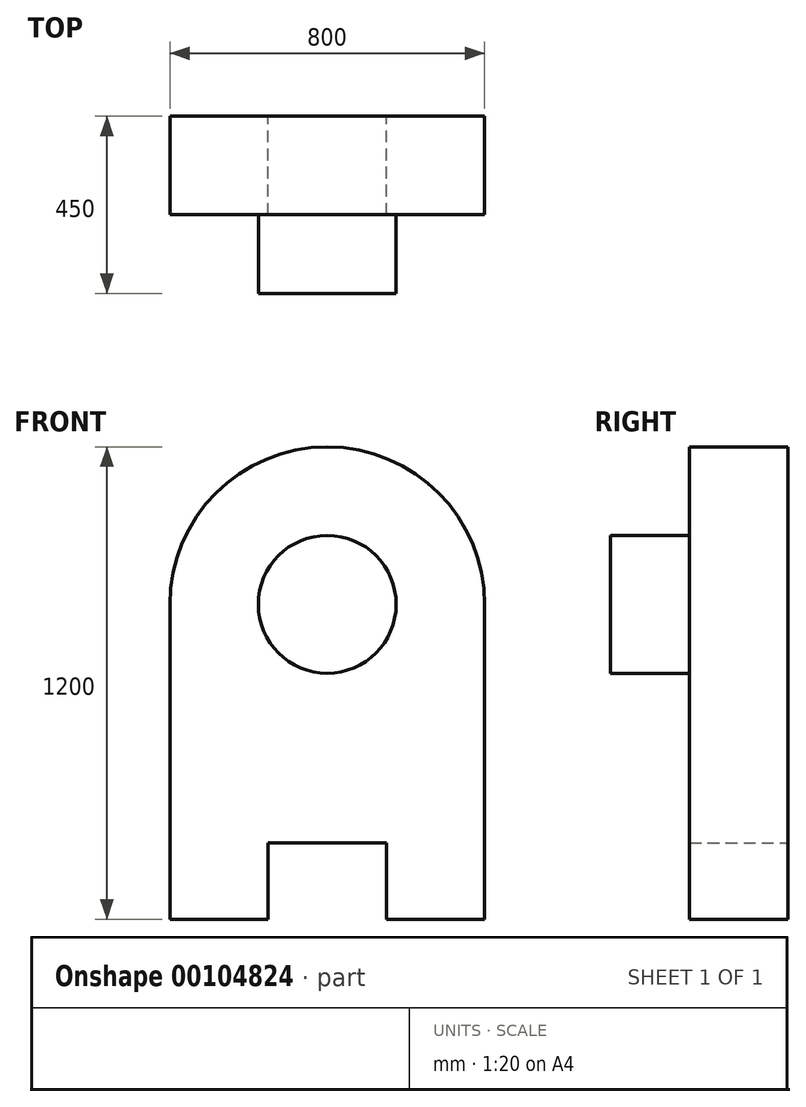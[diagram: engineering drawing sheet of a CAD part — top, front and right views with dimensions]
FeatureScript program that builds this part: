
annotation { "Feature Type Name" : "Feature", "Feature Type Description" : "" }
export const myFeature = defineFeature(function(context is Context, id is Id, definition is map)
    precondition{}
    {
        {
            var Q0;
            Q0=qCreatedBy(makeId("Front.planeOp"),FACE);
            var sketch = newSketch(context, id + "F0", { "sketchPlane" : qUnion([Q0])});
            skArc(sketch, "E0", {"start": v(400, 0) * mm, "mid": v(0, 400) * mm, "end": v(-400, 0) * mm});
            skLineSegment(sketch, "E1.bottom", {"start": v(-400, -800) * mm, "end": v(-150, -800) * mm});
            skLineSegment(sketch, "E1.left", {"start": v(-400, -800) * mm, "end": v(-400, 0) * mm});
            skLineSegment(sketch, "E1.right", {"start": v(400, -800) * mm, "end": v(400, 0) * mm});
            skPoint(sketch, "E1.top.end.orphan", {"position": v(400, 800) * mm});
            skPoint(sketch, "E2.orphan", {"position": v(-400, 800) * mm});
            skLineSegment(sketch, "E3", {"start": v(-150, -800) * mm, "end": v(-150, -606.18) * mm});
            skLineSegment(sketch, "E4", {"start": v(-150, -606.18) * mm, "end": v(150, -606.18) * mm});
            skLineSegment(sketch, "E5", {"start": v(150, -606.18) * mm, "end": v(150, -800) * mm});
            skPoint(sketch, "E6.end.orphan", {"position": v(168.48, -800) * mm});
            skLineSegment(sketch, "E7", {"start": v(150, -800) * mm, "end": v(400, -800) * mm});
            skSolve(sketch);
        }
        {
            var Q0;
            Q0 = qSketchRegion(id + "F0", true);
            extrude(context, id + "F1", {"entities" : qUnion([Q0]), "depth" : 250 * mm});
        }
        {
            var Q0;
            Q0=makeQuery(id+"F1.opExtrude","CAP_FACE",FACE,{"disambiguationData":[OSD([sQuery(id+"F0.wireOp",EDGE,"E0"),sQuery(id+"F0.wireOp",EDGE,"E1.bottom"),sQuery(id+"F0.wireOp",EDGE,"E1.left"),sQuery(id+"F0.wireOp",EDGE,"E1.right"),sQuery(id+"F0.wireOp",EDGE,"E3"),sQuery(id+"F0.wireOp",EDGE,"E4"),sQuery(id+"F0.wireOp",EDGE,"E5"),sQuery(id+"F0.wireOp",EDGE,"E7")])],"isStart":false});
            var sketch = newSketch(context, id + "F2", { "sketchPlane" : qUnion([Q0])});
            skCircle(sketch, "E8", {"center": v(0, 0) * mm, "radius": 175 * mm});
            skSolve(sketch);
        }
        {
            var Q0;
            Q0 = qSketchRegion(id + "F2", true);
            extrude(context, id + "F3", {"entities" : qUnion([Q0]), "operationType" : NewBodyOperationType.ADD, "depth" : 200 * mm});
        }
    });
